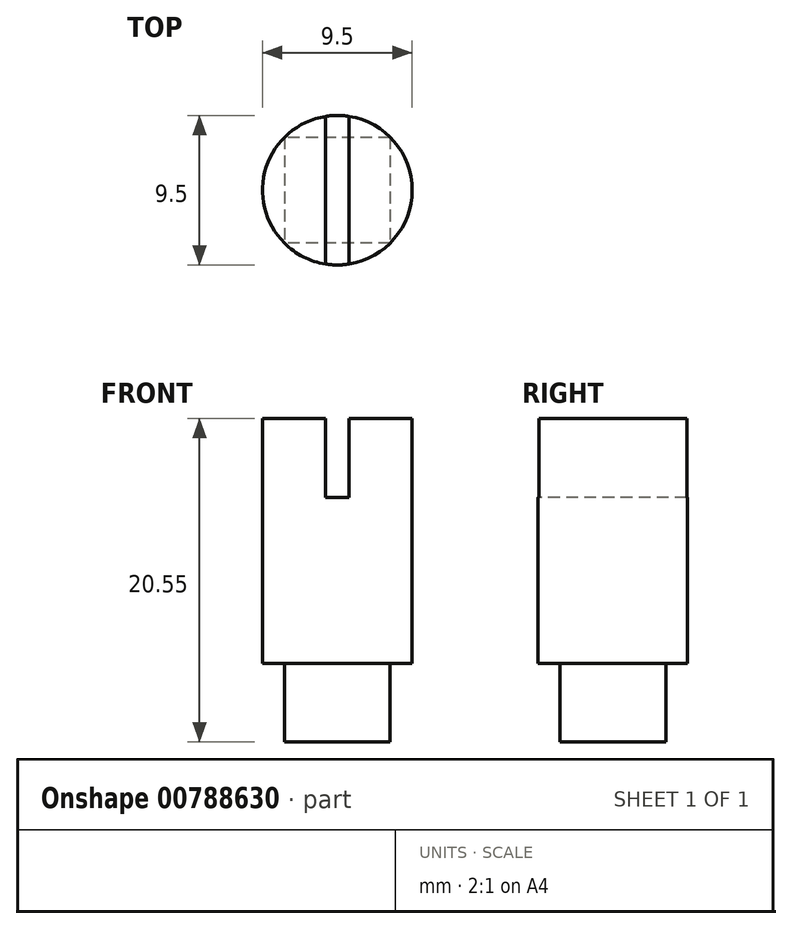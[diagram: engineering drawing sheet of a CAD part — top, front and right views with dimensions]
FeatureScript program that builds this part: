
annotation { "Feature Type Name" : "Feature", "Feature Type Description" : "" }
export const myFeature = defineFeature(function(context is Context, id is Id, definition is map)
    precondition{}
    {
        {
            var Q0;
            Q0=qCreatedBy(makeId("Top.planeOp"),FACE);
            var sketch = newSketch(context, id + "F0", { "sketchPlane" : qUnion([Q0])});
            skCircle(sketch, "E0", {"center": v(0, 0) * mm, "radius": 4.75 * mm});
            skSolve(sketch);
        }
        {
            var Q0;
            Q0=qSketchRegion(id+"F0",true);
            extrude(context, id + "F1", {"entities" : qUnion([Q0]), "depth" : 20.55 * mm, "offsetDistance" : 25.4 * mm});
        }
        {
            var Q0;
            Q0=qCreatedBy(makeId("Top.planeOp"),FACE);
            cPlane(context, id + "F2", {"entities" : qUnion([Q0]), "cplaneType" : CPlaneType.OFFSET, "offset" : 20.55 * mm, "width" : 152.4 * mm, "height" : 152.4 * mm});
        }
        {
            var Q0;
            Q0=qCreatedBy(id+"F2.planeOp",FACE);
            var sketch = newSketch(context, id + "F3", { "sketchPlane" : qUnion([Q0])});
            skLineSegment(sketch, "E1.bottom", {"start": v(0.75, 5.36) * mm, "end": v(-0.75, 5.36) * mm});
            skLineSegment(sketch, "E1.top", {"start": v(0.75, -5.36) * mm, "end": v(-0.75, -5.36) * mm});
            skLineSegment(sketch, "E1.left", {"start": v(0.75, 5.36) * mm, "end": v(0.75, -5.36) * mm});
            skLineSegment(sketch, "E1.right", {"start": v(-0.75, 5.36) * mm, "end": v(-0.75, -5.36) * mm});
            skPoint(sketch, "E1.middle", {"position": v(0, 0) * mm});
            skSolve(sketch);
        }
        {
            var Q0;
            Q0=qCreatedBy(makeId("Top.planeOp"),FACE);
            var sketch = newSketch(context, id + "F4", { "sketchPlane" : qUnion([Q0])});
            skLineSegment(sketch, "E2.bottom", {"start": v(4.8, 4.8) * mm, "end": v(-4.8, 4.8) * mm});
            skLineSegment(sketch, "E2.top", {"start": v(4.8, -4.8) * mm, "end": v(-4.8, -4.8) * mm});
            skLineSegment(sketch, "E2.left", {"start": v(4.8, 4.8) * mm, "end": v(4.8, -4.8) * mm});
            skLineSegment(sketch, "E2.right", {"start": v(-4.8, 4.8) * mm, "end": v(-4.8, -4.8) * mm});
            skPoint(sketch, "E2.middle", {"position": v(0, 0) * mm});
            skSolve(sketch);
        }
        {
            var Q0;
            Q0=qSketchRegion(id+"F4",true);
            extrude(context, id + "F5", {"entities" : qUnion([Q0]), "operationType" : NewBodyOperationType.REMOVE, "depth" : 5 * mm, "offsetDistance" : 25.4 * mm});
        }
        {
            var Q0;
            Q0=qSketchRegion(id+"F3",true);
            extrude(context, id + "F6", {"entities" : qUnion([Q0]), "operationType" : NewBodyOperationType.REMOVE, "oppositeDirection" : true, "depth" : 5 * mm, "offsetDistance" : 25.4 * mm});
        }
        {
            var Q0;
            Q0=qCreatedBy(makeId("Top.planeOp"),FACE);
            var sketch = newSketch(context, id + "F7", { "sketchPlane" : qUnion([Q0])});
            skLineSegment(sketch, "E3.bottom", {"start": v(3.36, 3.36) * mm, "end": v(-3.36, 3.36) * mm});
            skLineSegment(sketch, "E3.top", {"start": v(3.36, -3.36) * mm, "end": v(-3.36, -3.36) * mm});
            skLineSegment(sketch, "E3.left", {"start": v(3.36, 3.36) * mm, "end": v(3.36, -3.36) * mm});
            skLineSegment(sketch, "E3.right", {"start": v(-3.36, 3.36) * mm, "end": v(-3.36, -3.36) * mm});
            skPoint(sketch, "E3.middle", {"position": v(0, 0) * mm});
            skSolve(sketch);
        }
        {
            var Q0;
            Q0=qSketchRegion(id+"F7",true);
            extrude(context, id + "F8", {"entities" : qUnion([Q0]), "operationType" : NewBodyOperationType.ADD, "depth" : 5 * mm, "offsetDistance" : 25.4 * mm});
        }
        {
            var Q0;
            Q0=qCreatedBy(makeId("Top.planeOp"),FACE);
            cPlane(context, id + "F9", {"entities" : qUnion([Q0]), "cplaneType" : CPlaneType.OFFSET, "offset" : 8.15 * mm, "width" : 152.4 * mm, "height" : 152.4 * mm});
        }
    });
